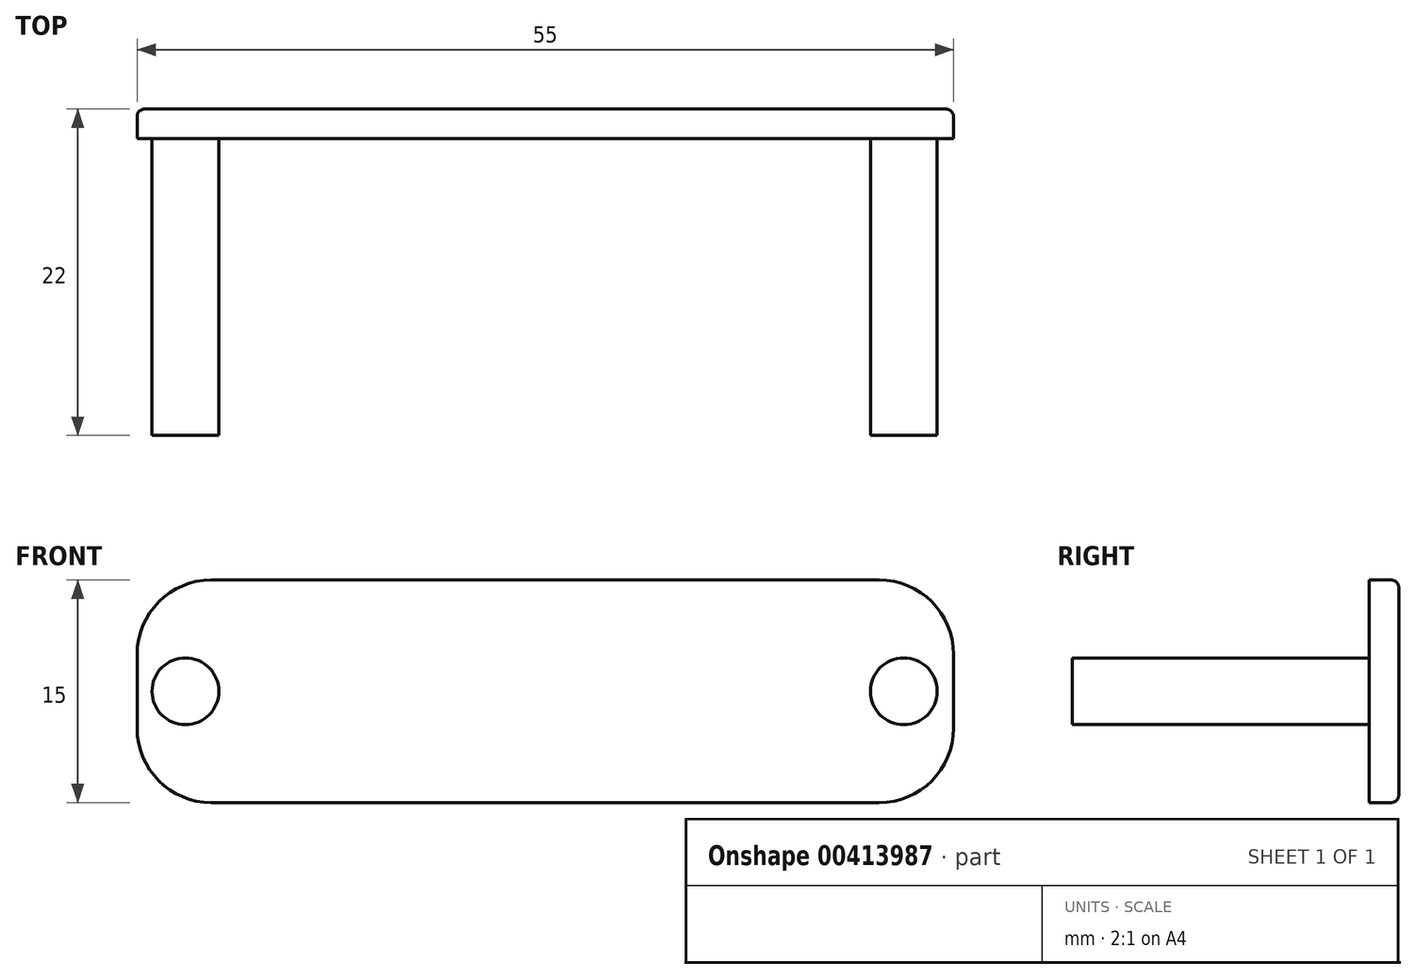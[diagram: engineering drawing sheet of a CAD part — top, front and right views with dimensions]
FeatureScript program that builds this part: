
annotation { "Feature Type Name" : "Feature", "Feature Type Description" : "" }
export const myFeature = defineFeature(function(context is Context, id is Id, definition is map)
    precondition{}
    {
        {
            var Q0;
            Q0=qCreatedBy(makeId("Front.planeOp"),FACE);
            var sketch = newSketch(context, id + "F0", { "sketchPlane" : qUnion([Q0])});
            skLineSegment(sketch, "E0.bottom", {"start": v(-22.5, 7.5) * mm, "end": v(22.5, 7.5) * mm});
            skLineSegment(sketch, "E0.top", {"start": v(-22.5, -7.5) * mm, "end": v(22.5, -7.5) * mm});
            skLineSegment(sketch, "E0.left", {"start": v(-27.5, 2.5) * mm, "end": v(-27.5, -2.5) * mm});
            skLineSegment(sketch, "E0.right", {"start": v(27.5, 2.5) * mm, "end": v(27.5, -2.5) * mm});
            skPoint(sketch, "E0.middle", {"position": v(0, 0) * mm});
            skPoint(sketch, "E1.visualSharp", {"position": v(-27.5, 7.5) * mm});
            skArc(sketch, "E1.filletArc", {"start": v(-22.5, 7.5) * mm, "mid": v(-26.04, 6.04) * mm, "end": v(-27.5, 2.5) * mm});
            skPoint(sketch, "E2.visualSharp", {"position": v(27.5, 7.5) * mm});
            skArc(sketch, "E2.filletArc", {"start": v(27.5, 2.5) * mm, "mid": v(26.04, 6.04) * mm, "end": v(22.5, 7.5) * mm});
            skPoint(sketch, "E3.visualSharp", {"position": v(27.5, -7.5) * mm});
            skArc(sketch, "E3.filletArc", {"start": v(22.5, -7.5) * mm, "mid": v(26.04, -6.04) * mm, "end": v(27.5, -2.5) * mm});
            skPoint(sketch, "E4.visualSharp", {"position": v(-27.5, -7.5) * mm});
            skArc(sketch, "E4.filletArc", {"start": v(-27.5, -2.5) * mm, "mid": v(-26.04, -6.04) * mm, "end": v(-22.5, -7.5) * mm});
            skSolve(sketch);
        }
        {
            var Q0;
            Q0 = qSketchRegion(id + "F0", true);
            extrude(context, id + "F1", {"entities" : qUnion([Q0]), "oppositeDirection" : true, "depth" : 2 * mm});
        }
        {
            var Q0;
            Q0=makeQuery(id+"F1.opExtrude","CAP_FACE",FACE,{"disambiguationData":[OSD([sQuery(id+"F0.wireOp",EDGE,"E0.bottom"),sQuery(id+"F0.wireOp",EDGE,"E0.top"),sQuery(id+"F0.wireOp",EDGE,"E0.left"),sQuery(id+"F0.wireOp",EDGE,"E0.right"),sQuery(id+"F0.wireOp",EDGE,"E1.filletArc"),sQuery(id+"F0.wireOp",EDGE,"E2.filletArc"),sQuery(id+"F0.wireOp",EDGE,"E3.filletArc"),sQuery(id+"F0.wireOp",EDGE,"E4.filletArc")])],"isStart":false});
            fillet(context, id + "F2", {"entities" : qUnion([Q0]), "radius" : .5 * mm, "tangentPropagation" : true, "allowEdgeOverflow" : false});
        }
        {
            var Q0;
            Q0=makeQuery(id+"F1.opExtrude","CAP_FACE",FACE,{"disambiguationData":[OSD([sQuery(id+"F0.wireOp",EDGE,"E0.bottom"),sQuery(id+"F0.wireOp",EDGE,"E0.top"),sQuery(id+"F0.wireOp",EDGE,"E0.left"),sQuery(id+"F0.wireOp",EDGE,"E0.right"),sQuery(id+"F0.wireOp",EDGE,"E1.filletArc"),sQuery(id+"F0.wireOp",EDGE,"E2.filletArc"),sQuery(id+"F0.wireOp",EDGE,"E3.filletArc"),sQuery(id+"F0.wireOp",EDGE,"E4.filletArc")])],"isStart":true});
            var sketch = newSketch(context, id + "F3", { "sketchPlane" : qUnion([Q0])});
            skCircle(sketch, "E5", {"center": v(24.16, 0) * mm, "radius": 2.25 * mm});
            skCircle(sketch, "E6.1.0.0", {"center": v(-24.24, 0) * mm, "radius": 2.25 * mm});
            skLineSegment(sketch, "E6.direction1", {"start": v(24.16, 0) * mm, "end": v(-24.24, 0) * mm, "construction": true});
            skSolve(sketch);
        }
        {
            var Q0;
            Q0=makeQuery(id+"F3.imprint","IMPRINT",FACE,{"disambiguationData":[TD([[makeQuery(id+"F3.imprint","IMPRINT",EDGE,{"derivedFrom":sQuery(id+"F3.wireOp",EDGE,"E5")}),1.0]])]});
            var Q1;
            Q1=makeQuery(id+"F3.imprint","IMPRINT",FACE,{"disambiguationData":[TD([[makeQuery(id+"F3.imprint","IMPRINT",EDGE,{"derivedFrom":sQuery(id+"F3.wireOp",EDGE,"E6.1.0.0")}),1.0]])]});
            extrude(context, id + "F4", {"entities" : qUnion([Q0, Q1]), "operationType" : NewBodyOperationType.ADD, "depth" : 20 * mm});
        }
    });
